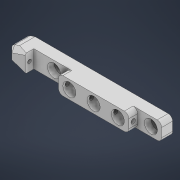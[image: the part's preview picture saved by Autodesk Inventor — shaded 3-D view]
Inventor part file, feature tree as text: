
AUTODESK INVENTOR PART (.ipt)
format: ipt  version: 2022 (Build 260153000, 153)  size: 256,000 bytes
history: native  units: mm
features: extrude x9, sketch x9, fillet x2, chamfer x1
ambient origin geometry x8: Origin, YZ Plane, XZ Plane, XY Plane, X Axis, Y Axis, Z Axis, Center Point
bodies: Solid1 (feature_tree)
feature tree (21):
  extrude  "Extrusion1"  Depth=11.0mm
  extrude  "Extrusion2"  Depth=8.0mm
  extrude  "Extrusion3"  Depth=4.0mm TaperAngle=0.0deg
  extrude  "Extrusion4"  Depth=15.0mm TaperAngle=0.0deg
  extrude  "Extrusion12"  Depth=2.0mm
  fillet  "Fillet5"  Radius=2.0mm
  chamfer  "Chamfer1"  Distance=15.0mm
  extrude  "Extrusion13"  Depth=2.0mm TaperAngle=45.0deg
  extrude  "Extrusion14"  Depth=2.0mm
  extrude  "Extrusion15"  Depth=2.0mm
  extrude  "Extrusion16"  Depth=10.0mm
  fillet  "Fillet6"  Radius=15.0mm
  sketch  "Sketch1"  dims[d0=66.0mm d1=11.0mm]
  sketch  "Sketch2"  dims[d2=5.0mm d3=0.0mm d4=8.0mm]
  sketch  "Sketch3"  dims[d5=10.0mm d6=4.0mm d7=0.0mm]
  sketch  "Sketch4"  dims[d9=50.0mm d10=0.0mm d16=15.0mm d17=0.0mm]
  sketch  "Sketch13"  dims[d63=2.0mm d64=2.0mm d65=2.0mm]
  sketch  "Sketch14"  dims[d66=2.0mm]
  sketch  "Sketch15"  dims[d68=2.8mm]
  sketch  "Sketch16"  dims[d69=2.8mm d70=15.0mm d71=0.0mm]
  sketch  "Sketch17"  dims[d72=2.0mm d73=2.0mm d74=2.0mm d75=45.0deg d76=4.85mm d77=3.5mm d78=50.0mm d80=11.0mm d81=10.0mm d83=10.0mm d85=15.0mm d86=0.0mm d87=1.5mm d88=1.5mm d89=15.0mm d90=0.0mm d91=5.9mm d92=2.0mm d93=5.9mm d94=2.0mm d95=4.0mm d96=0.0mm d97=5.9mm d98=5.9mm d99=8.0mm d100=0.0mm d101=3.0mm d102=0.0mm d103=2.0mm d104=1.7mm]
